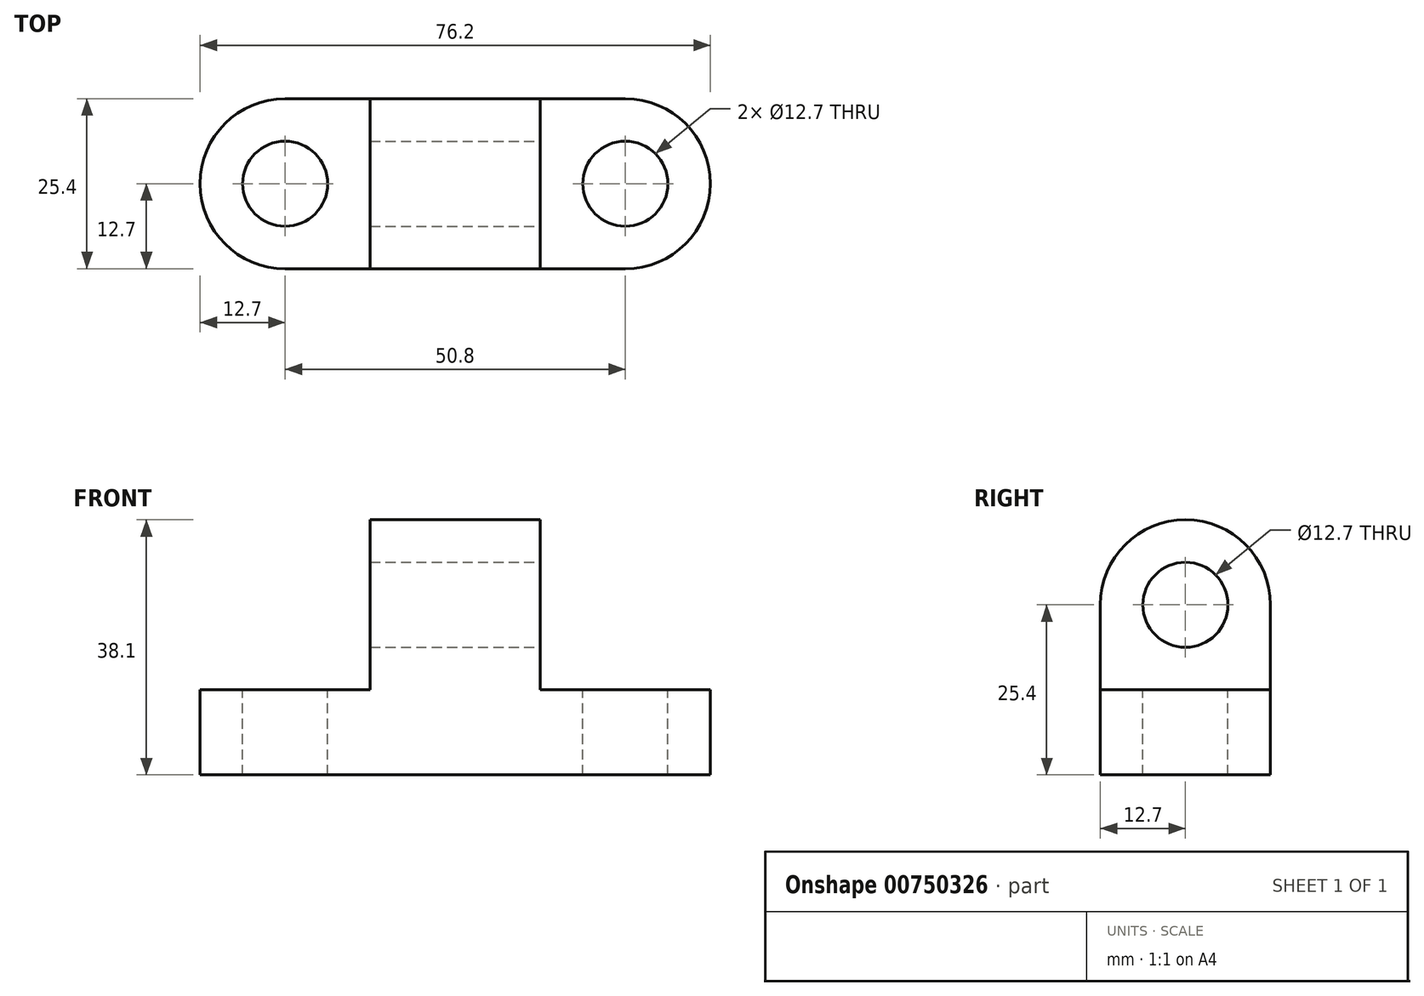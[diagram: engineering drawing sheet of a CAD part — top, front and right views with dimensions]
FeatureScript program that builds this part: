
annotation { "Feature Type Name" : "Feature", "Feature Type Description" : "" }
export const myFeature = defineFeature(function(context is Context, id is Id, definition is map)
    precondition{}
    {
        {
            var Q0;
            Q0=qCreatedBy(makeId("Front.planeOp"),FACE);
            var sketch = newSketch(context, id + "F0", { "sketchPlane" : qUnion([Q0])});
            skLineSegment(sketch, "E0", {"start": v(0, 0) * mm, "end": v(0, 12.7) * mm});
            skLineSegment(sketch, "E1", {"start": v(0, 12.7) * mm, "end": v(25.4, 12.7) * mm});
            skLineSegment(sketch, "E2", {"start": v(25.4, 12.7) * mm, "end": v(25.4, 38.1) * mm});
            skLineSegment(sketch, "E3", {"start": v(25.4, 38.1) * mm, "end": v(50.8, 38.1) * mm});
            skLineSegment(sketch, "E4", {"start": v(50.8, 38.1) * mm, "end": v(50.8, 12.7) * mm});
            skLineSegment(sketch, "E5", {"start": v(50.8, 12.7) * mm, "end": v(76.2, 12.7) * mm});
            skLineSegment(sketch, "E6", {"start": v(76.2, 12.7) * mm, "end": v(76.2, 0) * mm});
            skLineSegment(sketch, "E7", {"start": v(76.2, 0) * mm, "end": v(0, 0) * mm});
            skSolve(sketch);
        }
        {
            var Q0;
            Q0=makeQuery(id+"F0.imprint","IMPRINT",FACE,{"disambiguationData":[TD([[makeQuery(id+"F0.imprint","IMPRINT",EDGE,{"derivedFrom":sQuery(id+"F0.wireOp",EDGE,"E0")}),-1.0]])]});
            extrude(context, id + "F1", {"entities" : qUnion([Q0]), "depth" : 25.4 * mm, "offsetDistance" : 25.4 * mm});
        }
        {
            var Q0;
            Q0=makeQuery(id+"F1.opExtrude","CAP_EDGE",EDGE,{"disambiguationData":[OSD([sQuery(id+"F0.wireOp",EDGE,"E6")])],"isStart":false});
            fillet(context, id + "F2", {"entities" : qUnion([Q0]), "radius" : 12.7 * mm, "tangentPropagation" : true, "allowEdgeOverflow" : false});
        }
        {
            var Q0;
            Q0=makeQuery(id+"F1.opExtrude","CAP_EDGE",EDGE,{"disambiguationData":[OSD([sQuery(id+"F0.wireOp",EDGE,"E6")])],"isStart":true});
            fillet(context, id + "F3", {"entities" : qUnion([Q0]), "radius" : 12.7 * mm, "tangentPropagation" : true, "allowEdgeOverflow" : false});
        }
        {
            var Q0;
            Q0=makeQuery(id+"F1.opExtrude","CAP_EDGE",EDGE,{"disambiguationData":[OSD([sQuery(id+"F0.wireOp",EDGE,"E0")])],"isStart":false});
            fillet(context, id + "F4", {"entities" : qUnion([Q0]), "radius" : 12.7 * mm, "tangentPropagation" : true, "allowEdgeOverflow" : false});
        }
        {
            var Q0;
            Q0=makeQuery(id+"F1.opExtrude","CAP_EDGE",EDGE,{"disambiguationData":[OSD([sQuery(id+"F0.wireOp",EDGE,"E0")])],"isStart":true});
            fillet(context, id + "F5", {"entities" : qUnion([Q0]), "radius" : 12.7 * mm, "tangentPropagation" : true, "allowEdgeOverflow" : false});
        }
        {
            var Q0;
            Q0=makeQuery(id+"F1.opExtrude","CAP_EDGE",EDGE,{"disambiguationData":[OSD([sQuery(id+"F0.wireOp",EDGE,"E3")])],"isStart":true});
            fillet(context, id + "F6", {"entities" : qUnion([Q0]), "radius" : 12.7 * mm, "tangentPropagation" : true, "allowEdgeOverflow" : false});
        }
        {
            var Q0;
            Q0=makeQuery(id+"F1.opExtrude","CAP_EDGE",EDGE,{"disambiguationData":[OSD([sQuery(id+"F0.wireOp",EDGE,"E3")])],"isStart":false});
            fillet(context, id + "F7", {"entities" : qUnion([Q0]), "radius" : 12.7 * mm, "tangentPropagation" : true, "allowEdgeOverflow" : false});
        }
        {
            var Q0;
            Q0=makeQuery(id+"F1.opExtrude","SWEPT_FACE",FACE,{"disambiguationData":[OSD([sQuery(id+"F0.wireOp",EDGE,"E4")])]});
            var sketch = newSketch(context, id + "F8", { "sketchPlane" : qUnion([Q0])});
            skCircle(sketch, "E8", {"center": v(-12.7, 25.4) * mm, "radius": 6.35 * mm});
            skSolve(sketch);
        }
        {
            var Q0;
            Q0=makeQuery(id+"F8.imprint","IMPRINT",FACE,{"disambiguationData":[TD([[makeQuery(id+"F8.imprint","IMPRINT",EDGE,{"derivedFrom":sQuery(id+"F8.wireOp",EDGE,"E8")}),1.0]])]});
            extrude(context, id + "F9", {"entities" : qUnion([Q0]), "operationType" : NewBodyOperationType.REMOVE, "oppositeDirection" : true, "depth" : 25.4 * mm, "offsetDistance" : 25.4 * mm});
        }
        {
            var Q0;
            Q0=makeQuery(id+"F1.opExtrude","SWEPT_FACE",FACE,{"disambiguationData":[OSD([sQuery(id+"F0.wireOp",EDGE,"E5")])]});
            var sketch = newSketch(context, id + "F10", { "sketchPlane" : qUnion([Q0])});
            skCircle(sketch, "E9", {"center": v(63.5, -12.7) * mm, "radius": 6.35 * mm});
            skSolve(sketch);
        }
        {
            var Q0;
            Q0 = qSketchRegion(id + "F10", true);
            extrude(context, id + "F11", {"entities" : qUnion([Q0]), "operationType" : NewBodyOperationType.REMOVE, "oppositeDirection" : true, "depth" : 25.4 * mm, "offsetDistance" : 25.4 * mm});
        }
        {
            var Q0;
            Q0=makeQuery(id+"F1.opExtrude","SWEPT_FACE",FACE,{"disambiguationData":[OSD([sQuery(id+"F0.wireOp",EDGE,"E1")])]});
            var sketch = newSketch(context, id + "F12", { "sketchPlane" : qUnion([Q0])});
            skCircle(sketch, "E10", {"center": v(12.7, -12.7) * mm, "radius": 6.35 * mm});
            skSolve(sketch);
        }
        {
            var Q0;
            Q0 = qSketchRegion(id + "F12", true);
            extrude(context, id + "F13", {"entities" : qUnion([Q0]), "operationType" : NewBodyOperationType.REMOVE, "oppositeDirection" : true, "depth" : 25.4 * mm, "offsetDistance" : 25.4 * mm});
        }
    });
